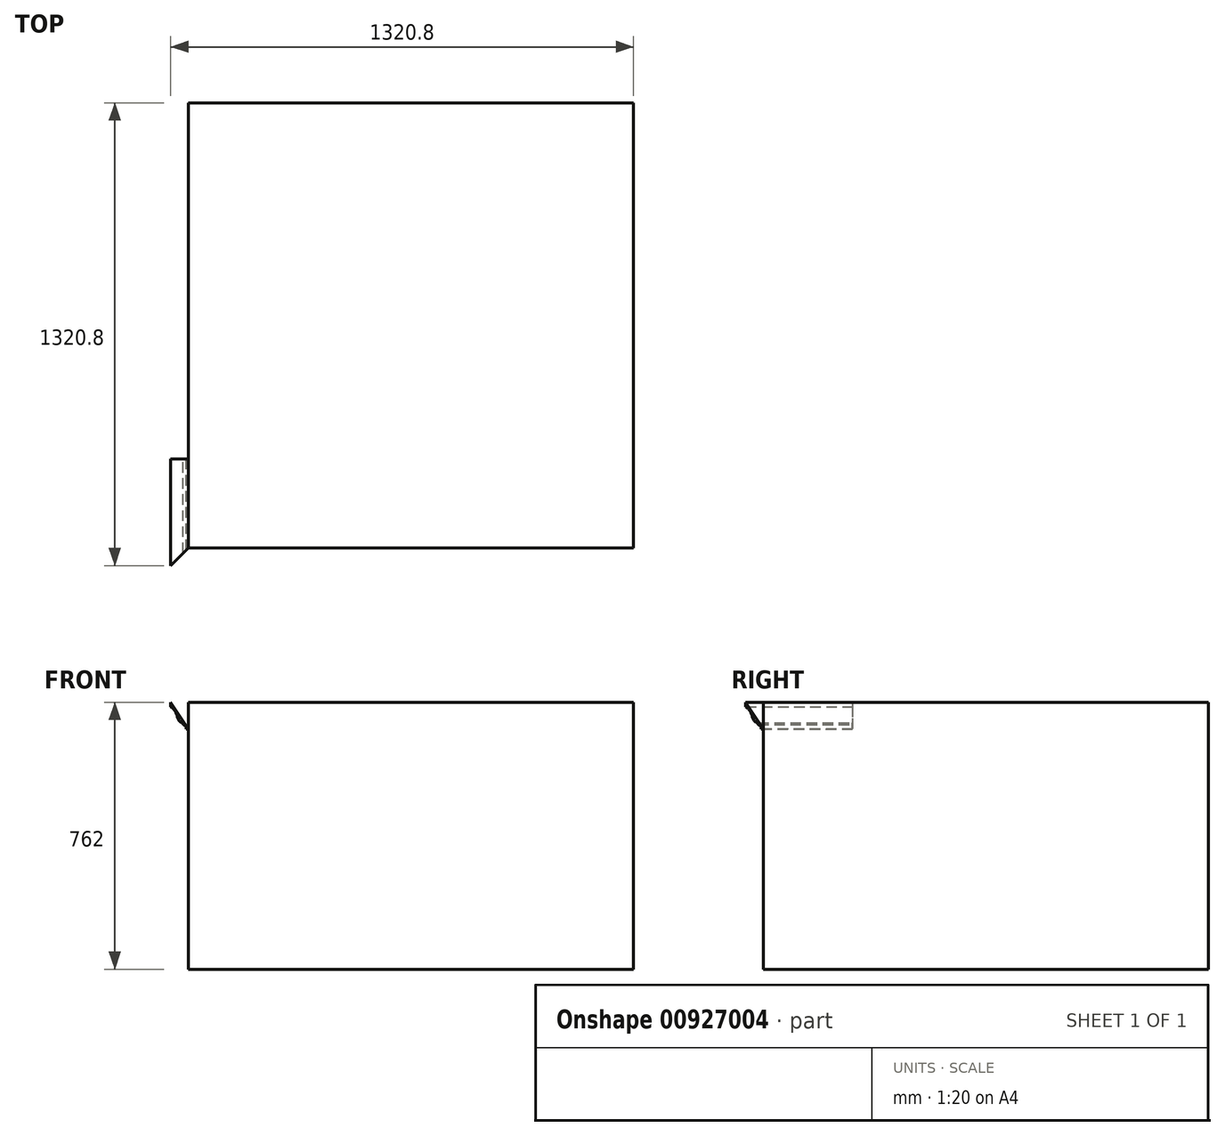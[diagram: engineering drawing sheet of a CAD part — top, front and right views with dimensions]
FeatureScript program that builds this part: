
annotation { "Feature Type Name" : "Feature", "Feature Type Description" : "" }
export const myFeature = defineFeature(function(context is Context, id is Id, definition is map)
    precondition{}
    {
        {
            var Q0;
            Q0=qCreatedBy(makeId("Top.planeOp"),FACE);
            var sketch = newSketch(context, id + "F0", { "sketchPlane" : qUnion([Q0])});
            skLineSegment(sketch, "E0.bottom", {"start": v(0, 0) * mm, "end": v(1270, 0) * mm});
            skLineSegment(sketch, "E0.top", {"start": v(0, 1270) * mm, "end": v(1270, 1270) * mm});
            skLineSegment(sketch, "E0.left", {"start": v(0, 0) * mm, "end": v(0, 1270) * mm});
            skLineSegment(sketch, "E0.right", {"start": v(1270, 0) * mm, "end": v(1270, 1270) * mm});
            skSolve(sketch);
        }
        {
            var Q0;
            Q0 = qSketchRegion(id + "F0", true);
            extrude(context, id + "F1", {"entities" : qUnion([Q0]), "depth" : 762 * mm, "offsetDistance" : 25.4 * mm});
        }
        {
            var Q0;
            Q0=makeQuery(id+"F1.opExtrude","SWEPT_EDGE",EDGE,{"disambiguationData":[OSD([sQuery(id+"F0.wireOp",EDGE,"E0.bottom"),sQuery(id+"F0.wireOp",EDGE,"E0.left")])]});
            cPlane(context, id + "F2", {"entities" : qUnion([Q0]), "cplaneType" : CPlaneType.LINE_ANGLE, "offset" : 25.4 * mm, "angle" : 45 * degree, "width" : 152.4 * mm, "height" : 152.4 * mm});
        }
        {
            var Q0;
            Q0=makeQuery(id+"F1.opExtrude","SWEPT_FACE",FACE,{"disambiguationData":[OSD([sQuery(id+"F0.wireOp",EDGE,"E0.bottom")])]});
            var sketch = newSketch(context, id + "F3", { "sketchPlane" : qUnion([Q0])});
            skLineSegment(sketch, "E1", {"start": v(-50.8, 762) * mm, "end": v(-44.45, 762) * mm, "construction": true});
            skLineSegment(sketch, "E2", {"start": v(0, 698.5) * mm, "end": v(0, 685.8) * mm, "construction": true});
            skLineSegment(sketch, "E3", {"start": v(-50.8, 762) * mm, "end": v(-50.8, 749.3) * mm});
            skLineSegment(sketch, "E4", {"start": v(0, 685.8) * mm, "end": v(-6.35, 685.8) * mm});
            skLineSegment(sketch, "E5", {"start": v(-44.45, 762) * mm, "end": v(0, 698.5) * mm, "construction": true});
            skFitSpline(sketch, "E6", {"points": [v(-6.35, 685.8) * mm, v(-8.5, 692.86) * mm, v(-15.4, 697.87) * mm], "startDerivative": vector(-2.3, 15.86) * mm, "endDerivative": vector(-15.64, 8.37) * mm});
            skLineSegment(sketch, "E7", {"start": v(-15.4, 697.87) * mm, "end": v(-15.4, 703.19) * mm});
            skFitSpline(sketch, "E8", {"points": [v(-50.8, 749.3) * mm, v(-36.86, 734.2) * mm, v(-27.76, 710.44) * mm, v(-15.4, 703.19) * mm], "startDerivative": vector(47.83, -35.44) * mm, "endDerivative": vector(52.53, -4.2) * mm});
            skLineSegment(sketch, "E9", {"start": v(-50.8, 762) * mm, "end": v(0, 685.8) * mm});
            skSolve(sketch);
        }
        {
            var Q0;
            Q0 = qSketchRegion(id + "F3", true);
            var Q1;
            Q1=sQuery(id+"F3.wireOp",EDGE,"Poq87JeU-IJud-fyQl-ilSS-nuBs98tdSdL8");
            var Q2;
            Q2=qCreatedBy(id+"F2.planeOp",FACE);
            extrude(context, id + "F4", {"entities" : qUnion([Q0]), "surfaceEntities" : qUnion([Q1]), "endBound" : BoundingType.UP_TO_SURFACE, "depth" : 25.4 * mm, "endBoundEntityFace" : qUnion([Q2]), "offsetDistance" : 25.4 * mm});
        }
        {
            var Q0;
            Q0=makeQuery(id+"F4.opExtrude","CAP_FACE",FACE,{"disambiguationData":[OSD([sQuery(id+"F3.wireOp",EDGE,"Poq87JeU-IJud-fyQl-ilSS-nuBs98tdSdL8"),sQuery(id+"F3.wireOp",EDGE,"E1"),sQuery(id+"F3.wireOp",EDGE,"2SeWliT3-ZfKl-tYEK-ITBJ-EU4OnpZea7zA"),sQuery(id+"F3.wireOp",EDGE,"E2")])],"isStart":true});
            var Q1;
            Q1=makeQuery(id+"F4.opExtrude","CAP_FACE",FACE,{"disambiguationData":[OSD([sQuery(id+"F3.wireOp",EDGE,"E3"),sQuery(id+"F3.wireOp",EDGE,"E4"),sQuery(id+"F3.wireOp",EDGE,"E6"),sQuery(id+"F3.wireOp",EDGE,"E7"),sQuery(id+"F3.wireOp",EDGE,"E8"),sQuery(id+"F3.wireOp",EDGE,"E9")])],"isStart":true});
            extrude(context, id + "F5", {"entities" : qUnion([Q0, Q1]), "operationType" : NewBodyOperationType.ADD, "depth" : 254 * mm, "offsetDistance" : 25.4 * mm});
        }
    });
